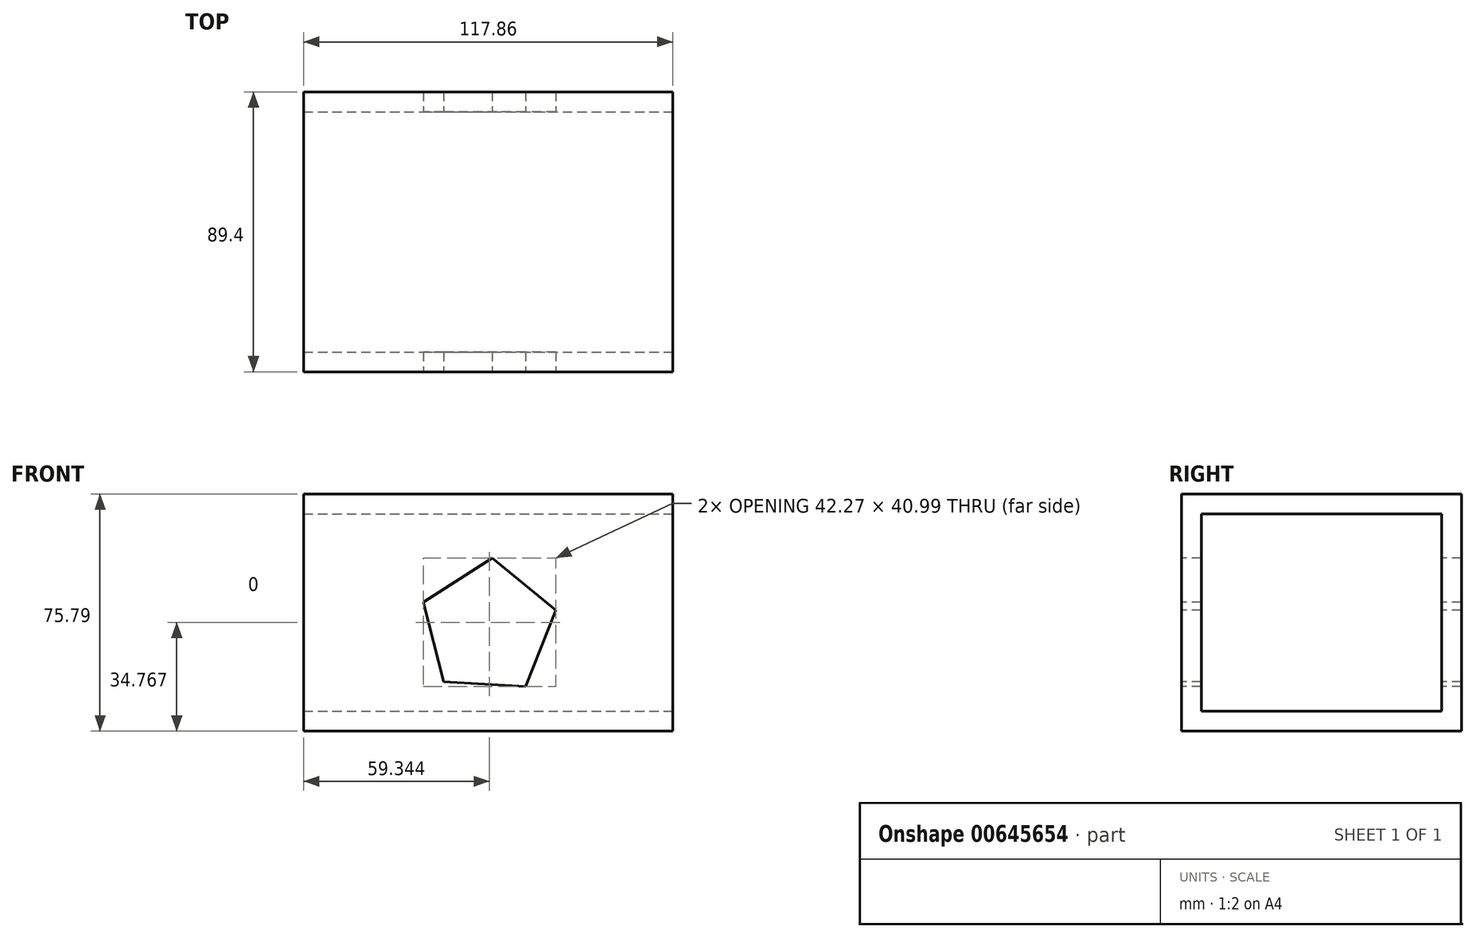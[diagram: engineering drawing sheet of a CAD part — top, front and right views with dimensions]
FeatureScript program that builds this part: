
annotation { "Feature Type Name" : "Feature", "Feature Type Description" : "" }
export const myFeature = defineFeature(function(context is Context, id is Id, definition is map)
    precondition{}
    {
        {
            var Q0;
            Q0=qCreatedBy(makeId("Right.planeOp"),FACE);
            var sketch = newSketch(context, id + "F0", { "sketchPlane" : qUnion([Q0])});
            skLineSegment(sketch, "E0.bottom", {"start": v(0, 42.75) * mm, "end": v(89.4, 42.75) * mm});
            skLineSegment(sketch, "E0.top", {"start": v(0, -33.04) * mm, "end": v(89.4, -33.04) * mm});
            skLineSegment(sketch, "E0.left", {"start": v(0, 42.75) * mm, "end": v(0, -33.04) * mm});
            skLineSegment(sketch, "E0.right", {"start": v(89.4, 42.75) * mm, "end": v(89.4, -33.04) * mm});
            skSolve(sketch);
        }
        {
            var Q0;
            Q0 = qSketchRegion(id + "F0", true);
            var sketch = newSketch(context, id + "F1", { "sketchPlane" : qUnion([Q0])});
            skSolve(sketch);
        }
        {
            var Q0;
            Q0 = qSketchRegion(id + "F1", true);
            var Q1;
            Q1=makeQuery(id+"F0.imprint","IMPRINT",FACE,{"disambiguationData":[TD([[makeQuery(id+"F0.imprint","IMPRINT",EDGE,{"derivedFrom":sQuery(id+"F0.wireOp",EDGE,"E0.bottom")}),-1.0]])]});
            extrude(context, id + "F2", {"entities" : qUnion([Q0, Q1]), "depth" : 117.86 * mm, "offsetDistance" : 25.4 * mm});
        }
        {
            var Q0;
            Q0=makeQuery(id+"F2.opExtrude","CAP_FACE",FACE,{"disambiguationData":[OSD([sQuery(id+"F0.wireOp",EDGE,"E0.bottom"),sQuery(id+"F0.wireOp",EDGE,"E0.top"),sQuery(id+"F0.wireOp",EDGE,"E0.left"),sQuery(id+"F0.wireOp",EDGE,"E0.right")])],"isStart":false});
            var sketch = newSketch(context, id + "F3", { "sketchPlane" : qUnion([Q0])});
            skLineSegment(sketch, "E1.0", {"start": v(6.35, 36.4) * mm, "end": v(83.05, 36.4) * mm});
            skLineSegment(sketch, "E1.1", {"start": v(6.35, 36.4) * mm, "end": v(6.35, -26.7) * mm});
            skLineSegment(sketch, "E1.2", {"start": v(6.35, -26.7) * mm, "end": v(83.05, -26.7) * mm});
            skLineSegment(sketch, "E1.3", {"start": v(83.05, 36.4) * mm, "end": v(83.05, -26.7) * mm});
            skSolve(sketch);
        }
        {
            var Q0;
            Q0=makeQuery(id+"F3.imprint","IMPRINT",FACE,{"disambiguationData":[TD([[makeQuery(id+"F3.imprint","IMPRINT",EDGE,{"derivedFrom":sQuery(id+"F3.wireOp",EDGE,"E1.0")}),-1.0]])]});
            extrude(context, id + "F4", {"entities" : qUnion([Q0]), "operationType" : NewBodyOperationType.REMOVE, "oppositeDirection" : true, "depth" : 168.55 * mm, "offsetDistance" : 25.4 * mm});
        }
        {
            var Q0;
            Q0=makeQuery(id+"F2.opExtrude","SWEPT_FACE",FACE,{"disambiguationData":[OSD([sQuery(id+"F0.wireOp",EDGE,"E0.left")])]});
            var sketch = newSketch(context, id + "F5", { "sketchPlane" : qUnion([Q0])});
            skCircle(sketch, "E2.cCircle", {"center": v(58.93, 0) * mm, "radius": 22.26 * mm, "construction": true});
            skPoint(sketch, "E2.cCircle.centerSnap0", {"position": v(58.93, 42.75) * mm});
            skLineSegment(sketch, "E2.0", {"start": v(80.48, 5.59) * mm, "end": v(70.9, -18.77) * mm});
            skLineSegment(sketch, "E2.1", {"start": v(70.9, -18.77) * mm, "end": v(44.78, -17.19) * mm});
            skLineSegment(sketch, "E2.2", {"start": v(44.78, -17.19) * mm, "end": v(38.2, 8.15) * mm});
            skLineSegment(sketch, "E2.3", {"start": v(38.2, 8.15) * mm, "end": v(60.27, 22.22) * mm});
            skLineSegment(sketch, "E2.4", {"start": v(60.27, 22.22) * mm, "end": v(80.48, 5.59) * mm});
            skSolve(sketch);
        }
        {
            var Q0;
            Q0=makeQuery(id+"F5.imprint","IMPRINT",FACE,{"disambiguationData":[TD([[makeQuery(id+"F5.imprint","IMPRINT",EDGE,{"derivedFrom":sQuery(id+"F5.wireOp",EDGE,"E2.0")}),-1.0]])]});
            var Q1;
            Q1 = qSketchRegion(id + "F5", true);
            extrude(context, id + "F6", {"entities" : qUnion([Q0, Q1]), "operationType" : NewBodyOperationType.REMOVE, "oppositeDirection" : true, "depth" : 108.43 * mm, "offsetDistance" : 25.4 * mm});
        }
    });
